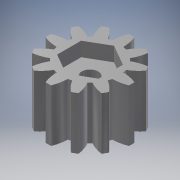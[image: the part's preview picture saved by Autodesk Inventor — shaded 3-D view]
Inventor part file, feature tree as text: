
AUTODESK INVENTOR PART (.ipt)
format: ipt  version: 2017 (Build 210142000, 142)  size: 211,968 bytes
history: native  units: mm (DEFAULTED — no unit token found)
features: sketch x5, extrude x3, plane x3, other x3
ambient origin geometry x8: Origin, YZ Plane, XZ Plane, XY Plane, X Axis, Y Axis, Z Axis, Center Point
bodies: Solid1 (feature_tree)
feature tree (14):
  extrude  "Extrusion1"  Depth=11.0mm TaperAngle=0.0deg
  plane  "Work Plane2"
  plane  "Work Plane8"
  plane  "Work Plane9"
  other  "Spur Gear"
  extrude  "Extrusion2"  Depth=10.0mm TaperAngle=0.0deg
  sketch  "Sketch4"  dims[d39=0.0mm]
  extrude  "Extrusion3"  TaperAngle=0.0deg  [1 undecoded]
  sketch  "Sketch1"  dims[d0=17.5mm d1=11.0mm d2=0.0mm]
  sketch  "Sketch2"  dims[d3=15.0mm d4=10.0mm d5=0.0mm]
  other  "Srf1"
  sketch  "Sketch3"  dims[d16=30.0mm d17=0.0mm d34=15.0deg]
  sketch  "Sketch5"  dims[d41=0.0mm d43=30.0mm d46=30.0mm d47=0.0mm d48=0.0mm d49=3.4544mm d50=15.0mm d51=0.0mm d52=10.0838mm d53=3.0mm d54=0.0mm]
  other  "Pitch Diameter"
note: 1 required parameter value undecoded (feature->parameter linkage not recoverable at this tier; creation-order binding heuristic only, values carry confidence <= 0.55)
